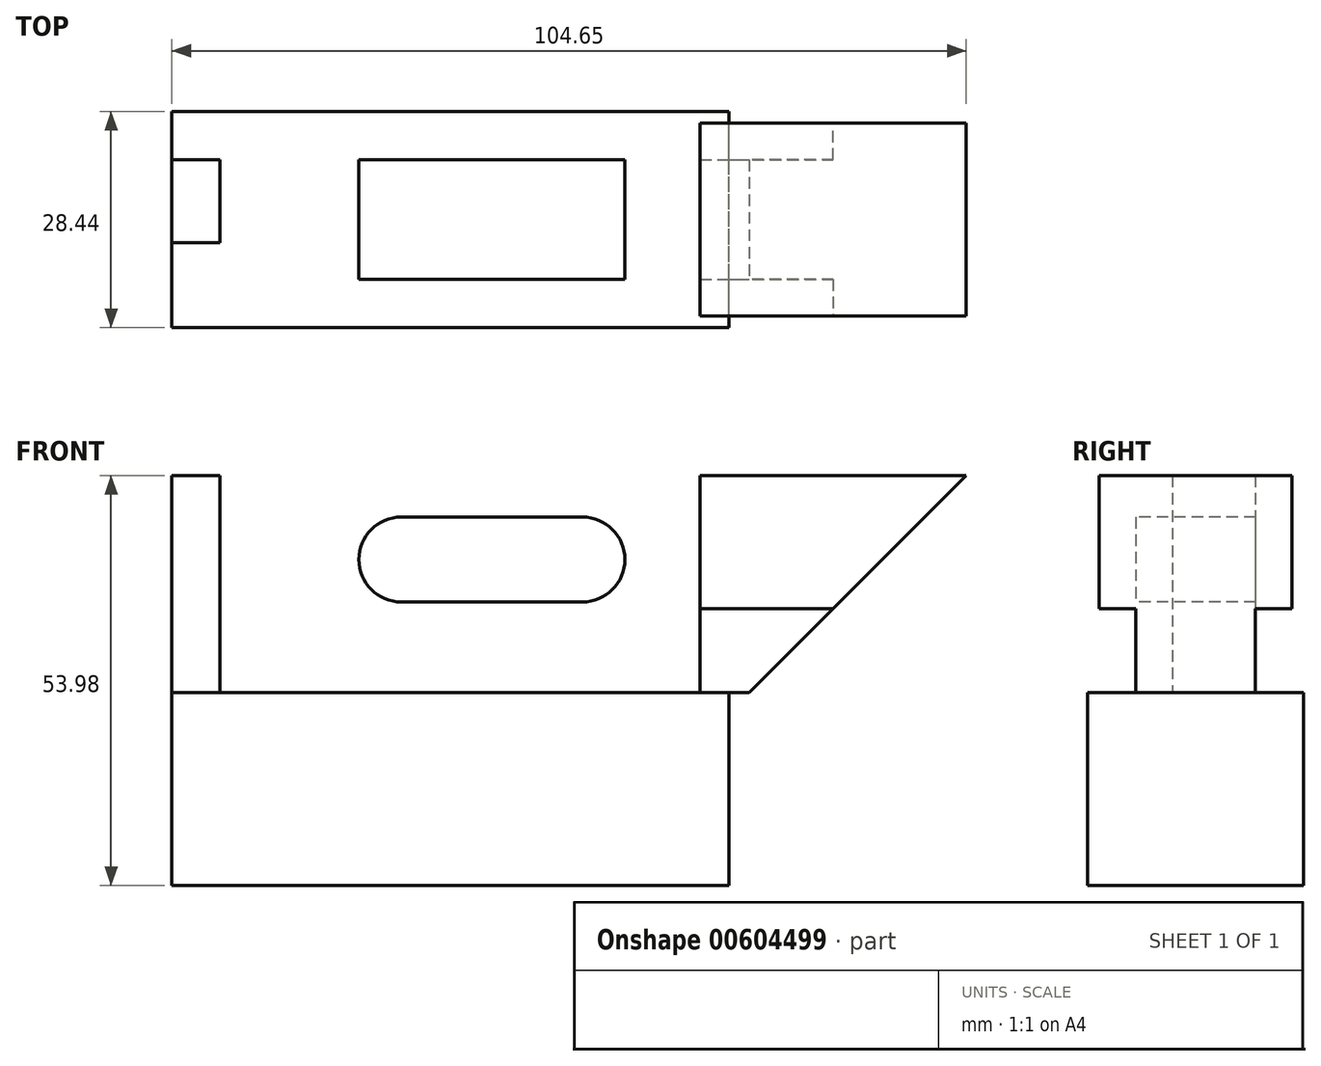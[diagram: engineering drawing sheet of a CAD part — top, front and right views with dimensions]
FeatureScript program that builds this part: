
annotation { "Feature Type Name" : "Feature", "Feature Type Description" : "" }
export const myFeature = defineFeature(function(context is Context, id is Id, definition is map)
    precondition{}
    {
        {
            var Q0;
            Q0=qCreatedBy(makeId("Front.planeOp"),FACE);
            var sketch = newSketch(context, id + "F0", { "sketchPlane" : qUnion([Q0])});
            skLineSegment(sketch, "E0.bottom", {"start": v(36.7, -12.7) * mm, "end": v(-36.7, -12.7) * mm});
            skLineSegment(sketch, "E0.top", {"start": v(36.7, 12.7) * mm, "end": v(-36.7, 12.7) * mm});
            skLineSegment(sketch, "E0.left", {"start": v(36.7, -12.7) * mm, "end": v(36.7, 12.7) * mm});
            skLineSegment(sketch, "E0.right", {"start": v(-36.7, -12.7) * mm, "end": v(-36.7, 12.7) * mm});
            skPoint(sketch, "E0.middle", {"position": v(0, 0) * mm});
            skSolve(sketch);
        }
        {
            var Q0;
            Q0=makeQuery(id+"F0.imprint","IMPRINT",FACE,{"disambiguationData":[TD([[makeQuery(id+"F0.imprint","IMPRINT",EDGE,{"derivedFrom":sQuery(id+"F0.wireOp",EDGE,"E0.bottom")}),-1.0]])]});
            extrude(context, id + "F1", {"entities" : qUnion([Q0]), "endBound" : BoundingType.SYMMETRIC, "depth" : 28.45 * mm, "offsetDistance" : 25.4 * mm});
        }
        {
            var Q0;
            Q0=makeQuery(id+"F1.opExtrude","SWEPT_FACE",FACE,{"disambiguationData":[OSD([sQuery(id+"F0.wireOp",EDGE,"E0.top")])]});
            var sketch = newSketch(context, id + "F2", { "sketchPlane" : qUnion([Q0])});
            skLineSegment(sketch, "E1.left", {"start": v(-36.7, -3.05) * mm, "end": v(-36.7, 7.87) * mm});
            skLineSegment(sketch, "E1.right", {"start": v(67.95, -12.7) * mm, "end": v(67.95, 12.7) * mm});
            skLineSegment(sketch, "E2", {"start": v(-36.7, 7.87) * mm, "end": v(32.9, 7.87) * mm});
            skLineSegment(sketch, "E3", {"start": v(32.9, 7.87) * mm, "end": v(32.9, 12.7) * mm});
            skLineSegment(sketch, "E4", {"start": v(-36.7, -3.05) * mm, "end": v(-30.35, -3.05) * mm});
            skLineSegment(sketch, "E5", {"start": v(-30.35, -3.05) * mm, "end": v(-30.35, -7.87) * mm});
            skLineSegment(sketch, "E6", {"start": v(-30.35, -7.87) * mm, "end": v(32.9, -7.87) * mm});
            skLineSegment(sketch, "E7", {"start": v(32.9, -7.87) * mm, "end": v(32.9, -12.7) * mm});
            skLineSegment(sketch, "E8", {"start": v(32.9, 12.7) * mm, "end": v(67.95, 12.7) * mm});
            skLineSegment(sketch, "E9", {"start": v(32.9, -12.7) * mm, "end": v(67.95, -12.7) * mm});
            skSolve(sketch);
        }
        {
            var Q0;
            Q0=makeQuery(id+"F2.imprint","IMPRINT",FACE,{"disambiguationData":[TD([[makeQuery(id+"F2.imprint","IMPRINT",EDGE,{"derivedFrom":sQuery(id+"F2.wireOp",EDGE,"E1.left")}),-1.0]])]});
            var Q1;
            {var subQ0=sQuery(id+"F2.wireOp",EDGE,"E1.right");Q1=makeQuery(id+"F2.imprint","IMPRINT",FACE,{"disambiguationData":[TD([[makeQuery(id+"F2.imprint","IMPRINT",EDGE,{"derivedFrom":subQ0}),1.0]])]});}
            extrude(context, id + "F3", {"entities" : qUnion([Q0, Q1]), "operationType" : NewBodyOperationType.ADD, "depth" : 28.57 * mm, "offsetDistance" : 25.4 * mm});
        }
        {
            var Q0;
            Q0=makeQuery(id+"F3.opExtrude","SWEPT_FACE",FACE,{"disambiguationData":[OSD([sQuery(id+"F2.wireOp",EDGE,"E6")])]});
            var sketch = newSketch(context, id + "F4", { "sketchPlane" : qUnion([Q0])});
            skLineSegment(sketch, "E10", {"start": v(-6.48, 30.23) * mm, "end": v(17.4, 30.23) * mm});
            skArc(sketch, "E11.0.startCap", {"start": v(-6.48, 24.64) * mm, "mid": v(-12.07, 30.23) * mm, "end": v(-6.48, 35.81) * mm});
            skArc(sketch, "E11.0.endCap", {"start": v(17.4, 35.81) * mm, "mid": v(22.99, 30.23) * mm, "end": v(17.4, 24.64) * mm});
            skLineSegment(sketch, "E11.0.left", {"start": v(-6.48, 35.81) * mm, "end": v(17.4, 35.81) * mm});
            skLineSegment(sketch, "E11.0.right", {"start": v(-6.48, 24.64) * mm, "end": v(17.4, 24.64) * mm});
            skSolve(sketch);
        }
        {
            var Q0;
            Q0=makeQuery(id+"F4.imprint","IMPRINT",FACE,{"disambiguationData":[TD([[makeQuery(id+"F4.imprint","IMPRINT",EDGE,{"derivedFrom":sQuery(id+"F4.wireOp",EDGE,"E11.0.startCap")}),-1.0]])]});
            extrude(context, id + "F5", {"entities" : qUnion([Q0]), "operationType" : NewBodyOperationType.REMOVE, "endBound" : BoundingType.THROUGH_ALL, "oppositeDirection" : true, "depth" : 25.4 * mm, "offsetDistance" : 25.4 * mm});
        }
        {
            var Q0;
            Q0=makeQuery(id+"F3.opExtrude","SWEPT_FACE",FACE,{"disambiguationData":[OSD([sQuery(id+"F2.wireOp",EDGE,"E1.right")])]});
            var sketch = newSketch(context, id + "F6", { "sketchPlane" : qUnion([Q0])});
            skLineSegment(sketch, "E12.bottom", {"start": v(-12.7, 12.7) * mm, "end": v(-7.87, 12.7) * mm});
            skLineSegment(sketch, "E12.top", {"start": v(-12.7, 23.75) * mm, "end": v(-7.87, 23.75) * mm});
            skLineSegment(sketch, "E12.left", {"start": v(-12.7, 12.7) * mm, "end": v(-12.7, 23.75) * mm});
            skLineSegment(sketch, "E12.right", {"start": v(-7.87, 12.7) * mm, "end": v(-7.87, 23.75) * mm});
            skLineSegment(sketch, "E13.bottom", {"start": v(12.7, 12.7) * mm, "end": v(7.87, 12.7) * mm});
            skLineSegment(sketch, "E13.top", {"start": v(12.7, 23.75) * mm, "end": v(7.87, 23.75) * mm});
            skLineSegment(sketch, "E13.left", {"start": v(12.7, 12.7) * mm, "end": v(12.7, 23.75) * mm});
            skLineSegment(sketch, "E13.right", {"start": v(7.87, 12.7) * mm, "end": v(7.87, 23.75) * mm});
            skSolve(sketch);
        }
        {
            var Q0;
            Q0=makeQuery(id+"F6.imprint","IMPRINT",FACE,{"disambiguationData":[TD([[makeQuery(id+"F6.imprint","IMPRINT",EDGE,{"derivedFrom":sQuery(id+"F6.wireOp",EDGE,"E12.bottom")}),1.0]])]});
            var Q1;
            Q1=makeQuery(id+"F6.imprint","IMPRINT",FACE,{"disambiguationData":[TD([[makeQuery(id+"F6.imprint","IMPRINT",EDGE,{"derivedFrom":sQuery(id+"F6.wireOp",EDGE,"E13.bottom")}),1.0]])]});
            extrude(context, id + "F7", {"entities" : qUnion([Q0, Q1]), "operationType" : NewBodyOperationType.REMOVE, "endBound" : BoundingType.THROUGH_ALL, "oppositeDirection" : true, "depth" : 25.4 * mm, "offsetDistance" : 25.4 * mm});
        }
        {
            var Q0;
            Q0=makeQuery(id+"F3.opExtrude","SWEPT_FACE",FACE,{"disambiguationData":[OSD([sQuery(id+"F2.wireOp",EDGE,"E9")])]});
            var sketch = newSketch(context, id + "F8", { "sketchPlane" : qUnion([Q0])});
            skLineSegment(sketch, "E14", {"start": v(39.37, 12.7) * mm, "end": v(67.95, 41.28) * mm});
            skLineSegment(sketch, "E15", {"start": v(67.95, 41.28) * mm, "end": v(67.95, 12.7) * mm});
            skLineSegment(sketch, "E16", {"start": v(67.95, 12.7) * mm, "end": v(39.37, 12.7) * mm});
            skSolve(sketch);
        }
        {
            var Q0;
            {var subQ0=sQuery(id+"F8.wireOp",EDGE,"E15");var subQ1=sQuery(id+"F8.wireOp",EDGE,"E14");var subQ2=sQuery(id+"F2.wireOp",EDGE,"E9");var subQ3=makeQuery(id+"F8.imprint","INTERSECT",VERTEX,{"derivedFrom":[makeQuery(id+"F3.opExtrude","CAP_EDGE",EDGE,{"disambiguationData":[OSD([subQ2])],"isStart":false}),subQ1,subQ0]});Q0=makeQuery(id+"F8.imprint","IMPRINT",FACE,{"disambiguationData":[TD([[makeQuery(id+"F8.imprint","IMPRINT",EDGE,{"disambiguationData":[TD([[subQ3,1.0]])],"derivedFrom":subQ1}),-1.0]])]});}
            var Q1;
            {var subQ0=sQuery(id+"F8.wireOp",EDGE,"E16");Q1=makeQuery(id+"F8.imprint","IMPRINT",FACE,{"disambiguationData":[TD([[makeQuery(id+"F8.imprint","IMPRINT",EDGE,{"derivedFrom":subQ0}),-1.0]])]});}
            extrude(context, id + "F9", {"entities" : qUnion([Q0, Q1]), "operationType" : NewBodyOperationType.REMOVE, "endBound" : BoundingType.THROUGH_ALL, "oppositeDirection" : true, "depth" : 25.4 * mm, "offsetDistance" : 25.4 * mm});
        }
    });
